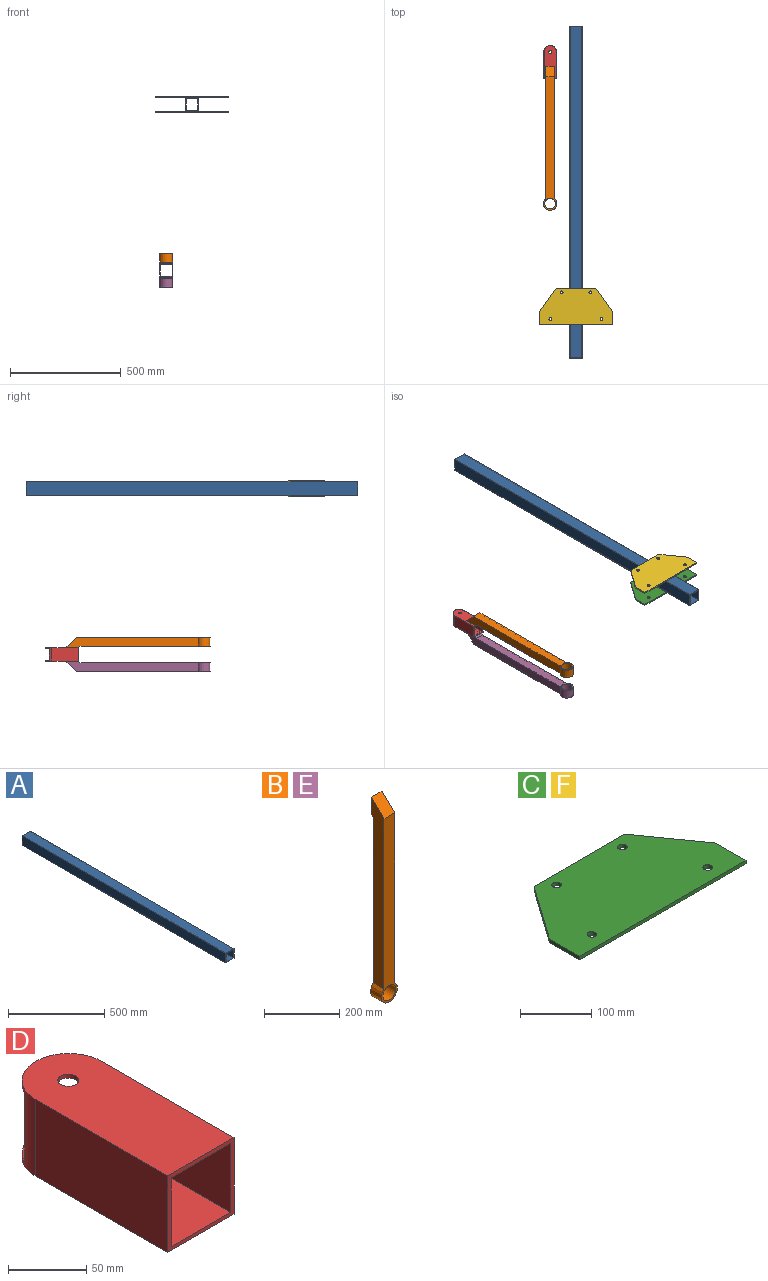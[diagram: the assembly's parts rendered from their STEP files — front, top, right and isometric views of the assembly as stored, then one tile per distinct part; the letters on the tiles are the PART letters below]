
ASSEMBLY  parts=6 mates=4
PART A: 10 faces, bbox 60x1500x60 mm
  f0: plane 1500x60mm, normal (0,0,1), area 90000mm2, adj f1,f7,f8,f9
  f1: plane 1500x60mm, normal (-1,0,0), area 90000mm2, adj f0,f2,f8,f9
  f2: plane 1500x60mm, normal (0,0,-1), area 90000mm2, adj f1,f7,f8,f9
  f3: plane 1500x54mm, normal (1,0,0), area 81000mm2, adj f4,f6,f8,f9
  f4: plane 1500x54mm, normal (0,0,-1), area 81000mm2, adj f3,f5,f8,f9
  f5: plane 1500x54mm, normal (-1,0,0), area 81000mm2, adj f4,f6,f8,f9
  f6: plane 1500x54mm, normal (0,0,1), area 81000mm2, adj f3,f5,f8,f9
  f7: plane 1500x60mm, normal (1,0,0), area 90000mm2, adj f0,f2,f8,f9
  f8: plane 60x60mm, normal (0,-1,0), area 684mm2, adj f0,f1,f2,f3,f4,f5,f6,f7
  f9: plane 60x60mm, normal (0,1,0), area 684mm2, adj f0,f1,f2,f3,f4,f5,f6,f7
PART B: 16 faces, bbox 60x47x651.1 mm
  f0: plane 32x11mm, normal (0,-0.71,0.71), area 497.8mm2, adj f2,f3,f8,f12
  f1: plane 43x43mm, normal (0,0.71,-0.71), area 1946mm2, adj f2,f3,f9,f12
  f2: plane 590.11x43mm, normal (1,0,0), area 18517.4mm2, adj f0,f1,f8,f9,f12,f13
  f3: plane 590.11x43mm, normal (-1,0,0), area 18517.4mm2, adj f0,f1,f8,f9,f12,f13
  f4: plane 40x7mm, normal (0,0.71,-0.71), area 396mm2, adj f6,f7,f10,f12
  f5: plane 47x47mm, normal (0,-0.71,0.71), area 2658.7mm2, adj f6,f7,f11,f12
  f6: plane 598.78x47mm, normal (-1,0,0), area 23267.4mm2, adj f4,f5,f10,f11,f12,f15
  f7: plane 598.78x47mm, normal (1,0,0), area 23267.4mm2, adj f4,f5,f10,f11,f12,f15
  f8: plane 533.86x32mm, normal (0,-1,0), area 16983.1mm2, adj f0,f2,f3,f13
  f9: plane 547.11x32mm, normal (0,1,0), area 17407.3mm2, adj f1,f2,f3,f13
  f10: plane 587.58x60.01mm, normal (0,1,0), area 22216.9mm2, adj f4,f6,f7,f14,f15
  f11: plane 604.15x60.01mm, normal (0,-1,0), area 22881.3mm2, adj f5,f6,f7,f14,f15
  f12: plane 56.57x40mm, normal (0,1,0), area 814.6mm2, adj f0,f1,f2,f3,f4,f5,f6,f7
  f13: cylinder r=30mm len=32mm, axis (0,1,0), area 1080.1mm2, adj f2,f3,f8,f9
  f14: cylinder r=24mm len=48mm, axis (0,1,0), area 6031.9mm2, adj f10,f11
  f15: extruded ~59.88x52.36mm, area 5788.8mm2, adj f6,f7,f10,f11
PART C: 12 faces, bbox 330.5x166x6 mm
  f0: plane 330.5x6mm, normal (0,-1,0), area 1983mm2, adj f1,f8,f10,f11
  f1: plane 60x6mm, normal (1,0,0), area 360mm2, adj f0,f2,f10,f11
  f2: plane 106x75mm, normal (0.82,0.58,0), area 779.1mm2, adj f1,f3,f10,f11
  f3: plane 180.5x6mm, normal (0,1,0), area 1083mm2, adj f2,f4,f10,f11
  f4: plane 106x75mm, normal (-0.82,0.58,0), area 779.1mm2, adj f3,f8,f10,f11
  f5: cylinder r=6.75mm len=13.5mm, axis (0,0,-1), area 254.5mm2, adj f10,f11
  f6: cylinder r=6.75mm len=13.5mm, axis (0,0,-1), area 254.5mm2, adj f10,f11
  f7: cylinder r=6.75mm len=13.5mm, axis (0,0,-1), area 254.5mm2, adj f10,f11
  f8: plane 60x6mm, normal (-1,0,0), area 360mm2, adj f0,f4,f10,f11
  f9: cylinder r=6.75mm len=13.5mm, axis (0,0,-1), area 254.5mm2, adj f10,f11
  f10: plane 330.5x166mm, normal (0,0,1), area 46340.4mm2, adj f0,f1,f2,f3,f4,f5,f6,f7
  f11: plane 330.5x166mm, normal (0,0,-1), area 46340.4mm2, adj f0,f1,f2,f3,f4,f5,f6,f7
PART D: 12 faces, bbox 60x149.5x60 mm
  f0: plane 149.5x60mm, normal (0,0,1), area 8440.7mm2, adj f1,f7,f8,f9,f11
  f1: plane 120x60mm, normal (-1,0,0), area 7200mm2, adj f0,f2,f8,f9
  f2: plane 149.5x60mm, normal (0,0,-1), area 8440.7mm2, adj f1,f7,f8,f9,f10
  f3: plane 132.58x54mm, normal (1,0,0), area 7159.4mm2, adj f4,f6,f8,f9
  f4: plane 149.5x54mm, normal (0,0,-1), area 7670.8mm2, adj f3,f5,f8,f9,f11
  f5: plane 132.58x54mm, normal (-1,0,0), area 7159.4mm2, adj f4,f6,f8,f9
  f6: plane 149.5x54mm, normal (0,0,1), area 7670.8mm2, adj f3,f5,f8,f9,f10
  f7: plane 120x60mm, normal (1,0,0), area 7200mm2, adj f0,f2,f8,f9
  f8: plane 60x60mm, normal (0,-1,0), area 684mm2, adj f0,f1,f2,f3,f4,f5,f6,f7
  f9: cylinder r=30mm len=60mm, axis (0,0,1), area 1967.5mm2, adj f0,f1,f2,f3,f4,f5,f6,f7
  f10: cylinder r=6.75mm len=13.5mm, axis (0,0,1), area 127.2mm2, adj f2,f6
  f11: cylinder r=6.75mm len=13.5mm, axis (0,0,1), area 127.2mm2, adj f0,f4
PART E: same geometry as B
PART F: same geometry as C
PLACE A at identity
PLACE B rot(axis=(-1,0,0),90deg) t=(-98.78,-779.15,-675.23)mm
PLACE C t=(1004.11,-646.18,-18.84)mm
PLACE D t=(227.01,-86.94,-621.14)mm
PLACE E rot(axis=(0,-0.71,-0.71),180deg) t=(-98.78,-779.15,-789.23)mm
PLACE F rot(axis=(0,1,0),180deg) t=(-968.31,-646.18,53.16)mm
MATE fastened B.f12 <-> D.f0  axis (0,0,-1) through (-98.78,-236.94,-702.23)mm
MATE fastened C.f10 <-> A.f2  axis (0,0,1) through (17.9,-1350,-12.84)mm
MATE fastened E.f12 <-> D.f2  axis (0,0,1) through (-98.78,-236.94,-762.23)mm
MATE fastened F.f10 <-> A.f0  axis (0,0,-1) through (17.9,-1350,47.16)mm
